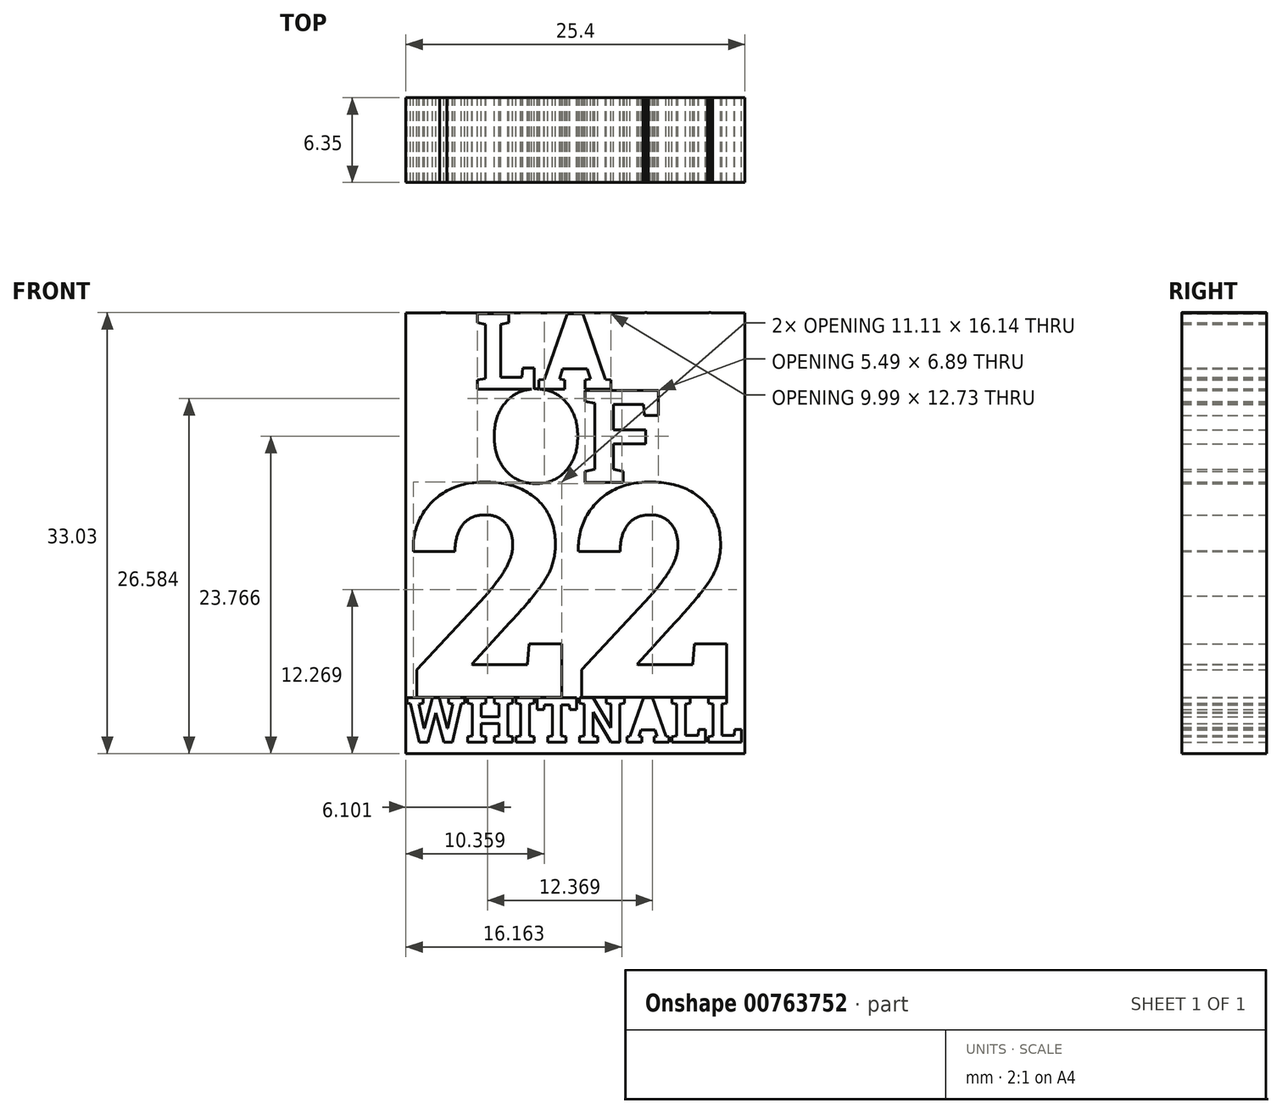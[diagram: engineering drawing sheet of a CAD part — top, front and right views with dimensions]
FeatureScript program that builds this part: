
annotation { "Feature Type Name" : "Feature", "Feature Type Description" : "" }
export const myFeature = defineFeature(function(context is Context, id is Id, definition is map)
    precondition{}
    {
        {
            var Q0;
            Q0=qCreatedBy(makeId("Front.planeOp"),FACE);
            var sketch = newSketch(context, id + "F0", { "sketchPlane" : qUnion([Q0])});
            skLineSegment(sketch, "E0", {"start": v(0, 0) * mm, "end": v(0, 33.02) * mm});
            skLineSegment(sketch, "E1", {"start": v(0, 33.02) * mm, "end": v(25.4, 33.02) * mm});
            skLineSegment(sketch, "E2", {"start": v(25.4, 33.02) * mm, "end": v(25.4, 0) * mm});
            skLineSegment(sketch, "E3", {"start": v(25.4, 0) * mm, "end": v(0, 0) * mm});
            skLineSegment(sketch, "E4", {"start": v(0, 33.02) * mm, "end": v(0, 20.32) * mm});
            skText(sketch, "E5", { "text": "CLASS", "fontName": "RobotoSlab-Bold.ttf"});
            skText(sketch, "E6", { "text": "OF", "fontName": "RobotoSlab-Bold.ttf"});
            skText(sketch, "E7", { "text": "22\n", "fontName": "RobotoSlab-Bold.ttf"});
            skText(sketch, "E8", { "text": "WHITNALL \n\n", "fontName": "RobotoSlab-Bold.ttf"});
            const initialGuessF0  = {"E5": [0, 0.0273, 1, 0, 0.00572], "E6": [0.0063, 0.02032, 1, 0, 0.00698], "E7": [0, 0.0042, 1, 0, 0.01611], "E8": [0, 0.00086, 1, 0, 0.00335]};
            skSetInitialGuess(sketch, initialGuessF0);
            skSolve(sketch);
        }
        {
            var Q0;
            Q0 = qSketchRegion(id + "F0", true);
            extrude(context, id + "F1", {"entities" : qUnion([Q0]), "depth" : 6.35 * mm, "offsetDistance" : 25.4 * mm});
        }
    });
